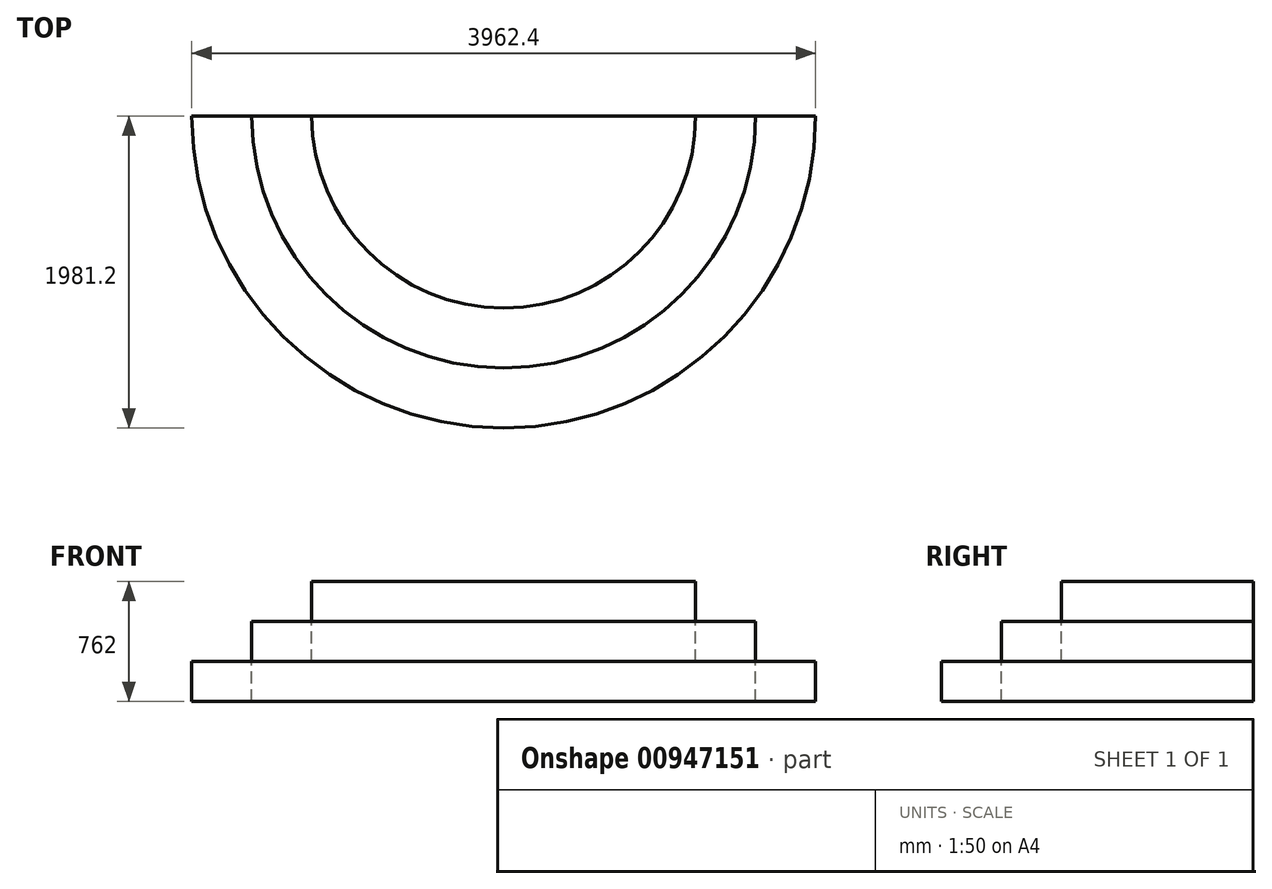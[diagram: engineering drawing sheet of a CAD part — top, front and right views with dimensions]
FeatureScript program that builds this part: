
annotation { "Feature Type Name" : "Feature", "Feature Type Description" : "" }
export const myFeature = defineFeature(function(context is Context, id is Id, definition is map)
    precondition{}
    {
        {
            var Q0;
            Q0=qCreatedBy(makeId("Top.planeOp"),FACE);
            var sketch = newSketch(context, id + "F0", { "sketchPlane" : qUnion([Q0])});
            skLineSegment(sketch, "E0.bottom", {"start": v(0, 0) * mm, "end": v(2438.4, 0) * mm});
            skArc(sketch, "E1", {"start": v(0, 0) * mm, "mid": v(1219.2, -1219.2) * mm, "end": v(2438.4, 0) * mm});
            skSolve(sketch);
        }
        {
            var Q0;
            Q0 = qSketchRegion(id + "F0", true);
            extrude(context, id + "F1", {"entities" : qUnion([Q0]), "depth" : 254 * mm, "offsetDistance" : 25.4 * mm});
        }
        {
            var Q0;
            Q0=makeQuery(id+"F1.opExtrude","CAP_FACE",FACE,{"disambiguationData":[OSD([sQuery(id+"F0.wireOp",EDGE,"E0.bottom"),sQuery(id+"F0.wireOp",EDGE,"E1")])],"isStart":true});
            var sketch = newSketch(context, id + "F2", { "sketchPlane" : qUnion([Q0])});
            skLineSegment(sketch, "E2", {"start": v(0, 0) * mm, "end": v(-381, 0) * mm});
            skLineSegment(sketch, "E3", {"start": v(2438.4, 0) * mm, "end": v(2819.4, 0) * mm});
            skArc(sketch, "E4", {"start": v(2819.4, 0) * mm, "mid": v(1219.2, 1600.2) * mm, "end": v(-381, 0) * mm});
            skSolve(sketch);
        }
        {
            var Q0;
            Q0 = qSketchRegion(id + "F2", true);
            var Q1;
            Q1=makeQuery(id+"F2.imprint","IMPRINT",FACE,{"disambiguationData":[TD([[makeQuery(id+"F2.imprint","IMPRINT",EDGE,{"derivedFrom":sQuery(id+"F2.wireOp",EDGE,"E2")}),-1.0]])]});
            extrude(context, id + "F3", {"entities" : qUnion([Q0, Q1]), "depth" : 254 * mm, "offsetDistance" : 25.4 * mm});
        }
        {
            var Q0;
            Q0=makeQuery(id+"F3.opExtrude","CAP_FACE",FACE,{"disambiguationData":[OSD([sQuery(id+"F0.wireOp",EDGE,"E1"),sQuery(id+"F2.wireOp",EDGE,"E2"),sQuery(id+"F2.wireOp",EDGE,"E3"),sQuery(id+"F2.wireOp",EDGE,"E4")])],"isStart":false});
            var sketch = newSketch(context, id + "F4", { "sketchPlane" : qUnion([Q0])});
            skLineSegment(sketch, "E5", {"start": v(-381, 0) * mm, "end": v(-762, 0) * mm});
            skLineSegment(sketch, "E6", {"start": v(2819.4, 0) * mm, "end": v(3200.4, 0) * mm});
            skArc(sketch, "E7", {"start": v(3200.4, 0) * mm, "mid": v(1219.2, 1981.2) * mm, "end": v(-762, 0) * mm});
            skSolve(sketch);
        }
        {
            var Q0;
            Q0 = qSketchRegion(id + "F4", true);
            var Q1;
            Q1=makeQuery(id+"F4.imprint","IMPRINT",FACE,{"disambiguationData":[TD([[makeQuery(id+"F4.imprint","IMPRINT",EDGE,{"derivedFrom":sQuery(id+"F4.wireOp",EDGE,"E5")}),-1.0]])]});
            extrude(context, id + "F5", {"entities" : qUnion([Q0, Q1]), "depth" : 254 * mm, "offsetDistance" : 25.4 * mm});
        }
    });
